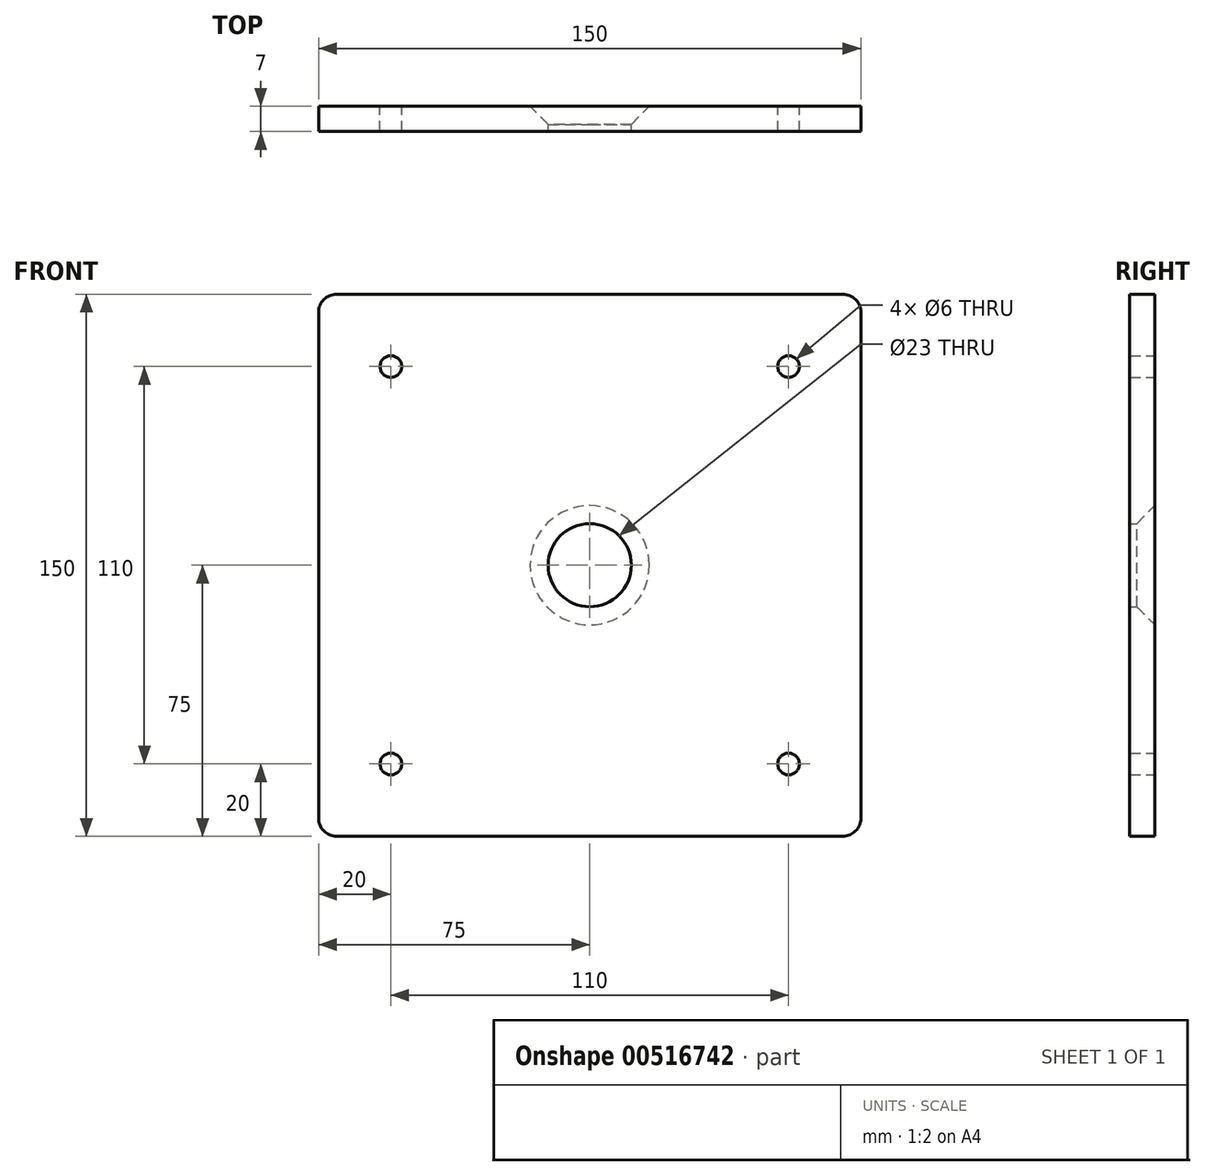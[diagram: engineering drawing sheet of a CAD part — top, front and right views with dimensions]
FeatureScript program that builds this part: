
annotation { "Feature Type Name" : "Feature", "Feature Type Description" : "" }
export const myFeature = defineFeature(function(context is Context, id is Id, definition is map)
    precondition{}
    {
        {
            var Q0;
            Q0=qCreatedBy(makeId("Front.planeOp"),FACE);
            var sketch = newSketch(context, id + "F0", { "sketchPlane" : qUnion([Q0])});
            skCircle(sketch, "E0", {"center": v(0, 0) * mm, "radius": 11.5 * mm});
            skCircle(sketch, "E1", {"center": v(-55, 55) * mm, "radius": 3 * mm});
            skCircle(sketch, "E2", {"center": v(55, 55) * mm, "radius": 3 * mm});
            skCircle(sketch, "E3", {"center": v(55, -55) * mm, "radius": 3 * mm});
            skCircle(sketch, "E4", {"center": v(-55, -55) * mm, "radius": 3 * mm});
            skLineSegment(sketch, "E5.bottom", {"start": v(-75, 75) * mm, "end": v(75, 75) * mm});
            skLineSegment(sketch, "E5.top", {"start": v(-75, -75) * mm, "end": v(75, -75) * mm});
            skLineSegment(sketch, "E5.left", {"start": v(-75, 75) * mm, "end": v(-75, -75) * mm});
            skLineSegment(sketch, "E5.right", {"start": v(75, 75) * mm, "end": v(75, -75) * mm});
            skSolve(sketch);
        }
        {
            var Q0;
            Q0 = qSketchRegion(id + "F0", true);
            extrude(context, id + "F1", {"entities" : qUnion([Q0]), "depth" : 7 * mm, "offsetDistance" : 25 * mm});
        }
        {
            var Q0;
            Q0=makeQuery(id+"F1.opExtrude","CAP_EDGE",EDGE,{"disambiguationData":[OSD([sQuery(id+"F0.wireOp",EDGE,"E0")])],"isStart":true});
            chamfer(context, id + "F2", {"entities" : qUnion([Q0]), "width" : 5 * mm, "tangentPropagation" : true});
        }
        {
            var Q0;
            Q0=makeQuery(id+"F1.opExtrude","SWEPT_EDGE",EDGE,{"disambiguationData":[OSD([sQuery(id+"F0.wireOp",EDGE,"E5.bottom"),sQuery(id+"F0.wireOp",EDGE,"E5.right")])]});
            var Q1;
            Q1=makeQuery(id+"F1.opExtrude","SWEPT_EDGE",EDGE,{"disambiguationData":[OSD([sQuery(id+"F0.wireOp",EDGE,"E5.bottom"),sQuery(id+"F0.wireOp",EDGE,"E5.left")])]});
            var Q2;
            Q2=makeQuery(id+"F1.opExtrude","SWEPT_EDGE",EDGE,{"disambiguationData":[OSD([sQuery(id+"F0.wireOp",EDGE,"E5.top"),sQuery(id+"F0.wireOp",EDGE,"E5.left")])]});
            var Q3;
            Q3=makeQuery(id+"F1.opExtrude","SWEPT_EDGE",EDGE,{"disambiguationData":[OSD([sQuery(id+"F0.wireOp",EDGE,"E5.top"),sQuery(id+"F0.wireOp",EDGE,"E5.right")])]});
            fillet(context, id + "F3", {"entities" : qUnion([Q0, Q1, Q2, Q3]), "radius" : 5 * mm, "tangentPropagation" : true, "allowEdgeOverflow" : false});
        }
    });
